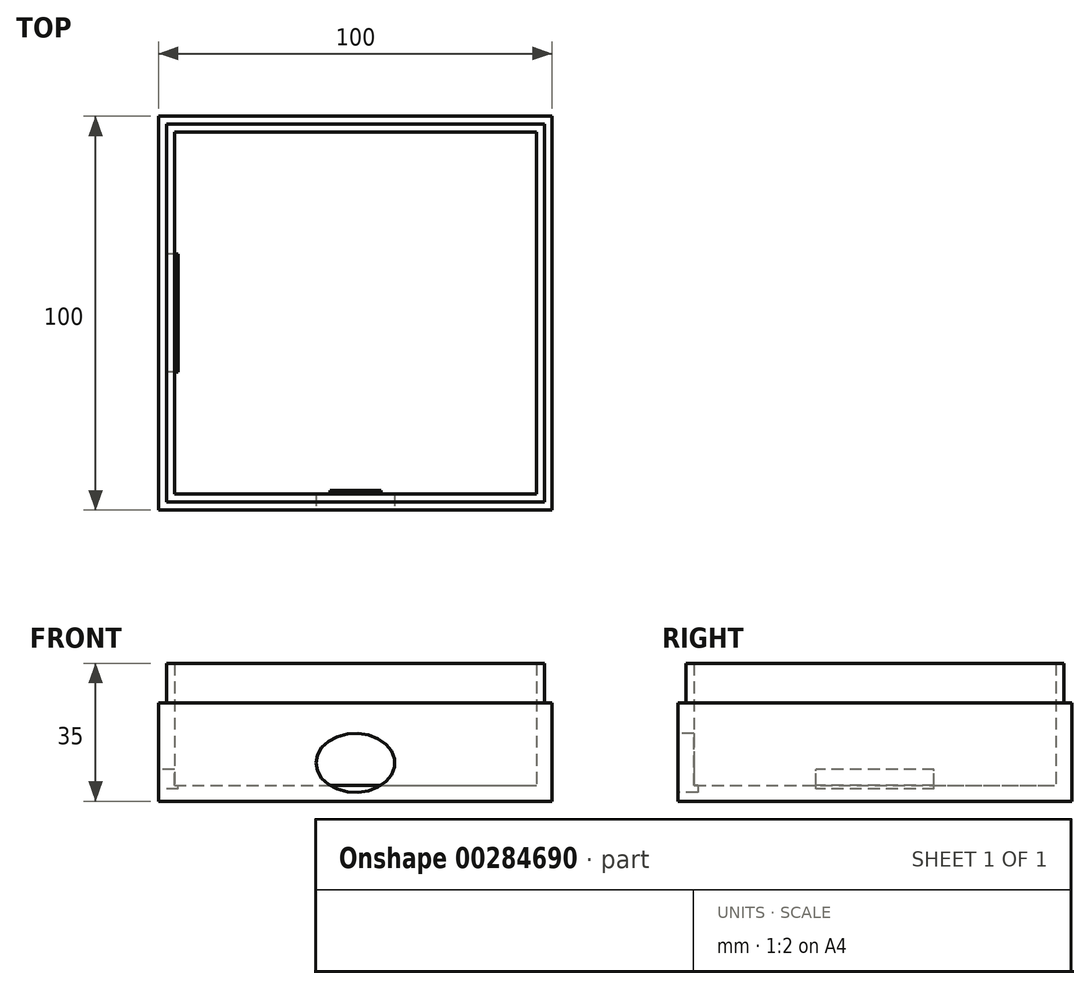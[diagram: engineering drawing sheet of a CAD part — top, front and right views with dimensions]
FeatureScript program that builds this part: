
annotation { "Feature Type Name" : "Feature", "Feature Type Description" : "" }
export const myFeature = defineFeature(function(context is Context, id is Id, definition is map)
    precondition{}
    {
        {
            var Q0;
            Q0=qCreatedBy(makeId("Top.planeOp"),FACE);
            var sketch = newSketch(context, id + "F0", { "sketchPlane" : qUnion([Q0])});
            skLineSegment(sketch, "E0.bottom", {"start": v(-50, -50) * mm, "end": v(50, -50) * mm});
            skLineSegment(sketch, "E0.top", {"start": v(-50, 50) * mm, "end": v(50, 50) * mm});
            skLineSegment(sketch, "E0.left", {"start": v(-50, -50) * mm, "end": v(-50, 50) * mm});
            skLineSegment(sketch, "E0.right", {"start": v(50, -50) * mm, "end": v(50, 50) * mm});
            skPoint(sketch, "E0.middle", {"position": v(0, 0) * mm});
            skSolve(sketch);
        }
        {
            var Q0;
            Q0=makeQuery(id+"F0.imprint","IMPRINT",FACE,{"disambiguationData":[TD([[makeQuery(id+"F0.imprint","IMPRINT",EDGE,{"derivedFrom":sQuery(id+"F0.wireOp",EDGE,"E0.bottom")}),1.0]])]});
            extrude(context, id + "F1", {"entities" : qUnion([Q0]), "depth" : 35 * mm});
        }
        {
            var Q0;
            Q0=makeQuery(id+"F1.opExtrude","CAP_FACE",FACE,{"disambiguationData":[OSD([sQuery(id+"F0.wireOp",EDGE,"E0.bottom"),sQuery(id+"F0.wireOp",EDGE,"E0.top"),sQuery(id+"F0.wireOp",EDGE,"E0.left"),sQuery(id+"F0.wireOp",EDGE,"E0.right")])],"isStart":false});
            shell(context, id + "F2", {"entities" : qUnion([Q0]), "thickness" : 4 * mm});
        }
        {
            var Q0;
            Q0=makeQuery(id+"F1.opExtrude","CAP_FACE",FACE,{"disambiguationData":[OSD([sQuery(id+"F0.wireOp",EDGE,"E0.bottom"),sQuery(id+"F0.wireOp",EDGE,"E0.top"),sQuery(id+"F0.wireOp",EDGE,"E0.left"),sQuery(id+"F0.wireOp",EDGE,"E0.right")])],"isStart":false});
            var sketch = newSketch(context, id + "F3", { "sketchPlane" : qUnion([Q0])});
            skLineSegment(sketch, "E1.bottom", {"start": v(-50, 50) * mm, "end": v(50, 50) * mm});
            skLineSegment(sketch, "E1.top", {"start": v(-48, 48) * mm, "end": v(48, 48) * mm});
            skLineSegment(sketch, "E1.left", {"start": v(-50, 50) * mm, "end": v(-50, 48) * mm});
            skLineSegment(sketch, "E1.right", {"start": v(50, 50) * mm, "end": v(50, 48) * mm});
            skLineSegment(sketch, "E2.bottom", {"start": v(50, 50) * mm, "end": v(48, 50) * mm});
            skLineSegment(sketch, "E2.top", {"start": v(50, -50) * mm, "end": v(48, -50) * mm});
            skLineSegment(sketch, "E2.left", {"start": v(50, 50) * mm, "end": v(50, -50) * mm});
            skLineSegment(sketch, "E2.right", {"start": v(48, 48) * mm, "end": v(48, -48) * mm});
            skLineSegment(sketch, "E3.bottom", {"start": v(50, -50) * mm, "end": v(-50, -50) * mm});
            skLineSegment(sketch, "E3.top", {"start": v(48, -48) * mm, "end": v(-48, -48) * mm});
            skLineSegment(sketch, "E3.left", {"start": v(50, -50) * mm, "end": v(50, -48) * mm});
            skLineSegment(sketch, "E3.right", {"start": v(-50, -50) * mm, "end": v(-50, -48) * mm});
            skLineSegment(sketch, "E4.bottom", {"start": v(-50, -50) * mm, "end": v(-48, -50) * mm});
            skLineSegment(sketch, "E4.top", {"start": v(-50, 50) * mm, "end": v(-48, 50) * mm});
            skLineSegment(sketch, "E4.left", {"start": v(-50, -50) * mm, "end": v(-50, 50) * mm});
            skLineSegment(sketch, "E4.right", {"start": v(-48, -48) * mm, "end": v(-48, 48) * mm});
            skSolve(sketch);
        }
        {
            var Q0;
            Q0 = qSketchRegion(id + "F3", true);
            extrude(context, id + "F4", {"entities" : qUnion([Q0]), "operationType" : NewBodyOperationType.REMOVE, "oppositeDirection" : true, "depth" : 10 * mm});
        }
        {
            var Q0;
            Q0=makeQuery(id+"F1.opExtrude","SWEPT_FACE",FACE,{"disambiguationData":[OSD([sQuery(id+"F0.wireOp",EDGE,"E0.left")])]});
            var sketch = newSketch(context, id + "F5", { "sketchPlane" : qUnion([Q0])});
            skLineSegment(sketch, "E5.bottom", {"start": v(-15, 3.11) * mm, "end": v(15, 3.11) * mm});
            skLineSegment(sketch, "E5.top", {"start": v(-15, 8.11) * mm, "end": v(15, 8.11) * mm});
            skLineSegment(sketch, "E5.left", {"start": v(-15, 3.11) * mm, "end": v(-15, 8.11) * mm});
            skLineSegment(sketch, "E5.right", {"start": v(15, 3.11) * mm, "end": v(15, 8.11) * mm});
            skPoint(sketch, "E5.middle", {"position": v(0, 5.61) * mm});
            skPoint(sketch, "E5.middle.positionSnap0", {"position": v(0, 0) * mm});
            skPoint(sketch, "E5.centerSnap0", {"position": v(0, 0) * mm});
            skSolve(sketch);
        }
        {
            var Q0;
            Q0 = qSketchRegion(id + "F5", true);
            extrude(context, id + "F6", {"entities" : qUnion([Q0]), "operationType" : NewBodyOperationType.REMOVE, "oppositeDirection" : true, "depth" : 5 * mm});
        }
        {
            var Q0;
            Q0=makeQuery(id+"F1.opExtrude","SWEPT_FACE",FACE,{"disambiguationData":[OSD([sQuery(id+"F0.wireOp",EDGE,"E0.bottom")])]});
            var sketch = newSketch(context, id + "F7", { "sketchPlane" : qUnion([Q0])});
            skEllipse(sketch, "E6", {"center": v(0, 9.72) * mm, "majorRadius": 10 * mm, "minorRadius": 7.5 * mm, "majorAxis": v(-1, 0)});
            skSolve(sketch);
        }
        {
            var Q0;
            Q0=makeQuery(id+"F7.imprint","IMPRINT",FACE,{"disambiguationData":[TD([[makeQuery(id+"F7.imprint","IMPRINT",EDGE,{"derivedFrom":sQuery(id+"F7.wireOp",EDGE,"E6")}),1.0]])]});
            extrude(context, id + "F8", {"entities" : qUnion([Q0]), "operationType" : NewBodyOperationType.REMOVE, "oppositeDirection" : true, "depth" : 5 * mm});
        }
    });
